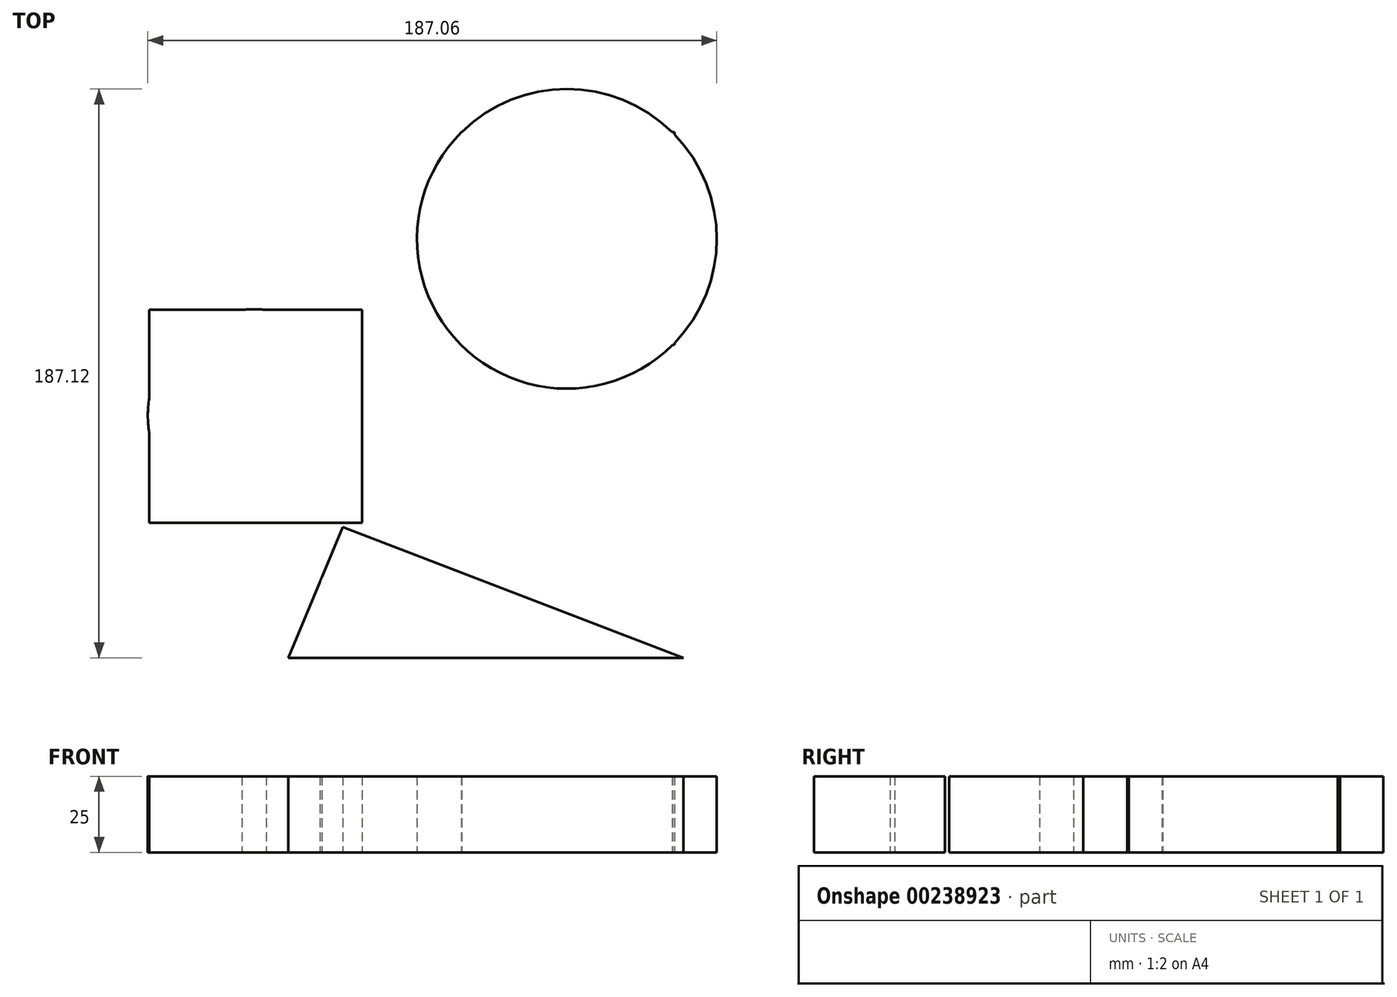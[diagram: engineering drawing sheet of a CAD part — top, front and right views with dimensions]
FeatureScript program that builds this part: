
annotation { "Feature Type Name" : "Feature", "Feature Type Description" : "" }
export const myFeature = defineFeature(function(context is Context, id is Id, definition is map)
    precondition{}
    {
        {
            var Q0;
            Q0=qCreatedBy(makeId("Top.planeOp"),FACE);
            var sketch = newSketch(context, id + "F0", { "sketchPlane" : qUnion([Q0])});
            skLineSegment(sketch, "E0", {"start": v(0, 20.9) * mm, "end": v(70, 20.9) * mm});
            skLineSegment(sketch, "E1.top", {"start": v(0, 90.9) * mm, "end": v(70, 90.9) * mm});
            skLineSegment(sketch, "E1.left", {"start": v(0, 20.9) * mm, "end": v(0, 90.9) * mm});
            skLineSegment(sketch, "E1.right", {"start": v(70, 20.9) * mm, "end": v(70, 90.9) * mm});
            skCircle(sketch, "E2", {"center": v(34.65, 55.81) * mm, "radius": 49.28 * mm});
            skLineSegment(sketch, "E3.bottom", {"start": v(-102.69, 32.44) * mm, "end": v(-32.69, 32.44) * mm});
            skLineSegment(sketch, "E3.top", {"start": v(-102.69, -37.56) * mm, "end": v(-32.69, -37.56) * mm});
            skLineSegment(sketch, "E3.left", {"start": v(-102.69, 32.44) * mm, "end": v(-102.69, -37.56) * mm});
            skLineSegment(sketch, "E3.right", {"start": v(-32.69, 32.44) * mm, "end": v(-32.69, -37.56) * mm});
            skCircle(sketch, "E4", {"center": v(-68.17, -2.3) * mm, "radius": 34.97 * mm});
            skLineSegment(sketch, "E5", {"start": v(-57, -82.02) * mm, "end": v(73, -82.02) * mm});
            skLineSegment(sketch, "E6", {"start": v(73, -82.02) * mm, "end": v(-39.02, -39.01) * mm});
            skLineSegment(sketch, "E7", {"start": v(-39.02, -39.01) * mm, "end": v(-57, -82.02) * mm});
            skCircle(sketch, "E8", {"center": v(-29.18, -63.4) * mm, "radius": 18.5 * mm});
            skSolve(sketch);
        }
        {
            var Q0;
            Q0 = qSketchRegion(id + "F0", true);
            extrude(context, id + "F1", {"entities" : qUnion([Q0]), "depth" : 25 * mm});
        }
    });
